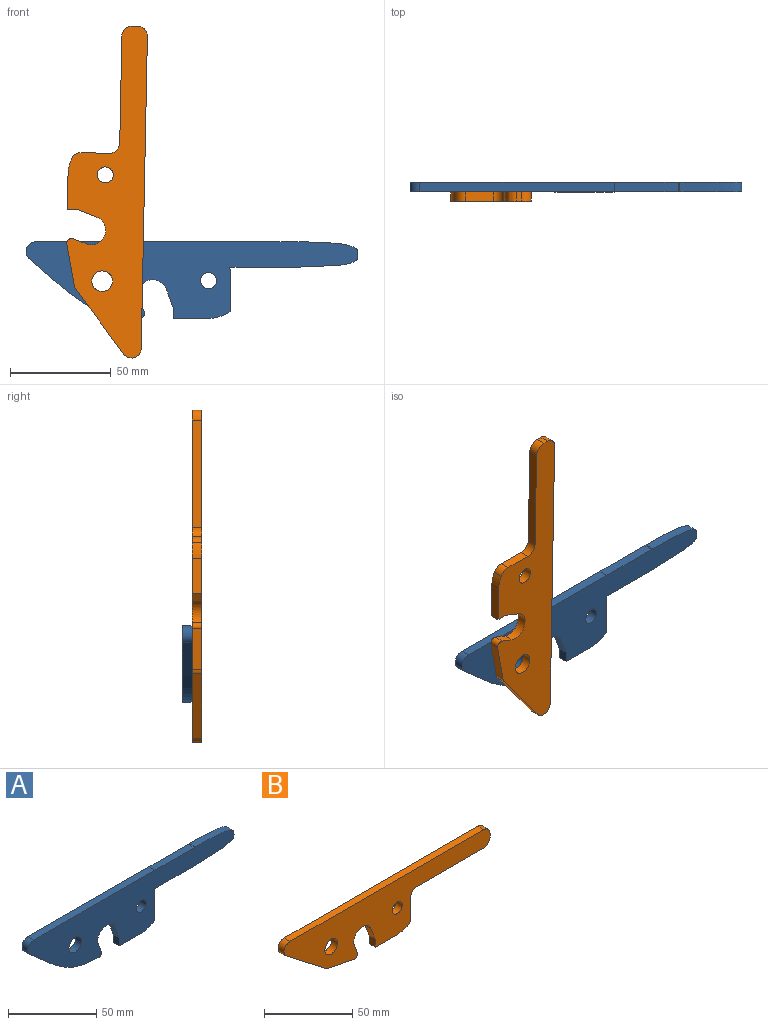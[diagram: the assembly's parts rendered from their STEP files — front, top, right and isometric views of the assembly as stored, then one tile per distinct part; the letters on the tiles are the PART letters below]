
ASSEMBLY  parts=2 mates=1
PART A: 19 faces, bbox 165.2x4.8x38.1 mm
  f0: extruded ~4.76x0.9mm, area 4.3mm2, adj f1,f15,f17,f18
  f1: plane 31.61x4.76mm, normal (0,0,1), area 150.5mm2, adj f0,f2,f17,f18
  f2: plane 96.94x4.76mm, normal (0,0,1), area 461.7mm2, adj f1,f3,f17,f18
  f3: cylinder r=4.76mm len=8.53mm, axis (0,1,0), area 56.3mm2, adj f2,f4,f17,f18
  f4: extruded ~54.16x29.44mm, area 302.3mm2, adj f3,f5,f17,f18
  f5: cylinder r=2.39mm len=4.76mm, axis (0,1,0), area 24.1mm2, adj f4,f6,f17,f18
  f6: plane 6.91x4.76mm, normal (0.94,0,0.35), area 35.1mm2, adj f5,f7,f17,f18
  f7: cylinder r=7.15mm len=13.84mm, axis (0,1,0), area 103.8mm2, adj f6,f8,f17,f18
  f8: plane 9.12x4.76mm, normal (-0.94,0,-0.35), area 46.4mm2, adj f7,f9,f17,f18
  f9: plane 5.51x4.76mm, normal (-1,0,0), area 26.2mm2, adj f8,f10,f17,f18
  f10: plane 17.62x4.76mm, normal (0,0,-1), area 83.9mm2, adj f9,f11,f17,f18
  f11: cylinder r=18.94mm len=10.79mm, axis (0,1,0), area 54.7mm2, adj f10,f12,f17,f18
  f12: plane 22.02x4.76mm, normal (1,0,0.01), area 104.9mm2, adj f11,f13,f17,f18
  f13: plane 31.89x4.76mm, normal (0,0,-1), area 151.9mm2, adj f12,f15,f17,f18
  f14: cylinder r=3.97mm len=7.94mm, axis (0,1,0), area 118.8mm2, adj f17,f18
  f15: extruded ~31.75x12.7mm, area 323.9mm2, adj f0,f13,f17,f18
  f16: cylinder r=5.16mm len=10.31mm, axis (0,1,0), area 154.3mm2, adj f17,f18
  f17: plane 165.2x38.1mm, normal (0,-1,0), area 3610mm2, adj f0,f1,f2,f3,f4,f5,f6,f7
  f18: plane 165.2x38.1mm, normal (0,1,0), area 3610mm2, adj f0,f1,f2,f3,f4,f5,f6,f7
PART B: 23 faces, bbox 165.1x4.8x38.1 mm
  f0: plane 155.22x4.76mm, normal (0,0,1), area 739.2mm2, adj f1,f16,f17,f22
  f1: cylinder r=4.76mm len=8.53mm, axis (0,1,0), area 56.3mm2, adj f0,f2,f16,f17
  f2: plane 31.5x24.4mm, normal (-0.61,0,-0.79), area 189.7mm2, adj f1,f16,f17,f18
  f3: plane 20.54x4.76mm, normal (-0.19,0,-0.98), area 99.7mm2, adj f4,f16,f17,f18
  f4: cylinder r=2.39mm len=4.76mm, axis (0,1,0), area 24.1mm2, adj f3,f5,f16,f17
  f5: plane 6.91x4.76mm, normal (0.94,0,0.35), area 35.1mm2, adj f4,f6,f16,f17
  f6: cylinder r=7.15mm len=13.84mm, axis (0,1,0), area 103.8mm2, adj f5,f7,f16,f17
  f7: plane 9.12x4.76mm, normal (-0.94,0,-0.35), area 46.4mm2, adj f6,f8,f16,f17
  f8: plane 5.51x4.76mm, normal (-1,0,0), area 26.2mm2, adj f7,f9,f16,f17
  f9: plane 17.62x4.76mm, normal (0,0,-1), area 83.9mm2, adj f8,f10,f16,f17
  f10: cylinder r=18.94mm len=7.81mm, axis (0,1,0), area 38.3mm2, adj f9,f16,f17,f19
  f11: plane 14.01x4.76mm, normal (1,0,0), area 66.7mm2, adj f16,f17,f19,f20
  f12: plane 53.34x4.76mm, normal (0,0,-1), area 254mm2, adj f16,f17,f20,f21
  f13: cylinder r=5.16mm len=10.31mm, axis (0,1,0), area 154.3mm2, adj f16,f17
  f14: plane 4.76x2.54mm, normal (1,0,0), area 12.1mm2, adj f16,f17,f21,f22
  f15: cylinder r=3.97mm len=7.94mm, axis (0,1,0), area 118.8mm2, adj f16,f17
  f16: plane 165.06x38.1mm, normal (0,-1,0), area 3598.6mm2, adj f0,f1,f2,f3,f4,f5,f6,f7
  f17: plane 165.06x38.1mm, normal (0,1,0), area 3598.6mm2, adj f0,f1,f2,f3,f4,f5,f6,f7
  f18: cylinder r=5.08mm len=4.76mm, axis (0,1,0), area 11.2mm2, adj f2,f3,f16,f17
  f19: cylinder r=5.08mm len=4.76mm, axis (0,1,0), area 27.7mm2, adj f10,f11,f16,f17
  f20: cylinder r=5.08mm len=5.08mm, axis (0,-1,0), area 38mm2, adj f11,f12,f16,f17
  f21: cylinder r=5.08mm len=5.08mm, axis (0,-1,0), area 38mm2, adj f12,f14,f16,f17
  f22: cylinder r=5.08mm len=5.08mm, axis (0,1,0), area 38mm2, adj f0,f14,f16,f17
PLACE A t=(-45.81,-53.64,-40.79)mm fixed
PLACE B rot(axis=(0.71,0,0.7),180deg) t=(-239.61,-63.17,157.32)mm
MATE revolute B.f13 <-> A.f16  axis (0,1,0) through (-81.26,-58.4,118.71)mm
